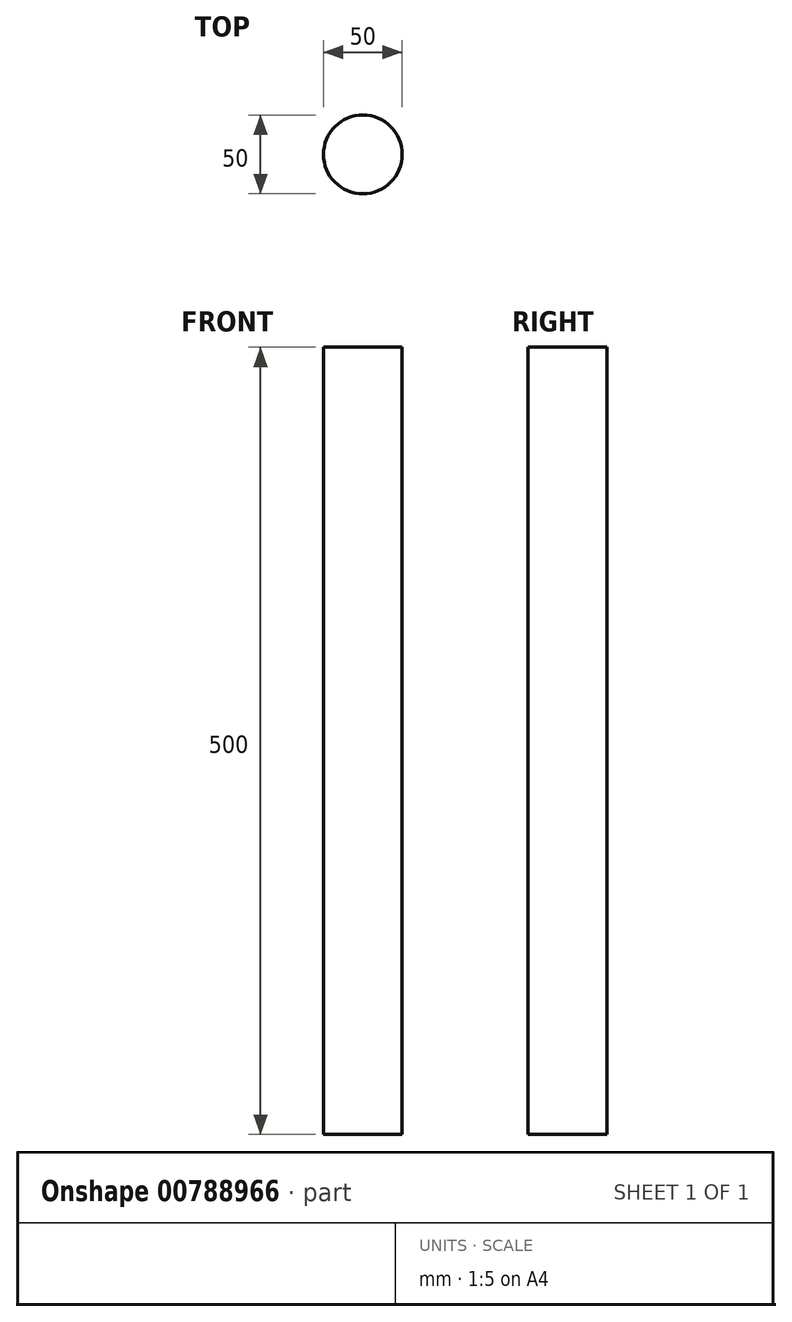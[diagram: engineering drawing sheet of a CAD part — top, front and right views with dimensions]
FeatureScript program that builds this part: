
annotation { "Feature Type Name" : "Feature", "Feature Type Description" : "" }
export const myFeature = defineFeature(function(context is Context, id is Id, definition is map)
    precondition{}
    {
        {
            var Q0;
            Q0=qCreatedBy(makeId("Top.planeOp"),FACE);
            var sketch = newSketch(context, id + "F0", { "sketchPlane" : qUnion([Q0])});
            skCircle(sketch, "E0", {"center": v(0, 0) * mm, "radius": 25 * mm});
            skSolve(sketch);
        }
        {
            var Q0;
            Q0=makeQuery(id+"F0.imprint","IMPRINT",FACE,{"disambiguationData":[TD([[makeQuery(id+"F0.imprint","IMPRINT",EDGE,{"derivedFrom":sQuery(id+"F0.wireOp",EDGE,"E0")}),1.0]])]});
            extrude(context, id + "F1", {"entities" : qUnion([Q0]), "depth" : 500 * mm, "offsetDistance" : 25 * mm});
        }
    });
